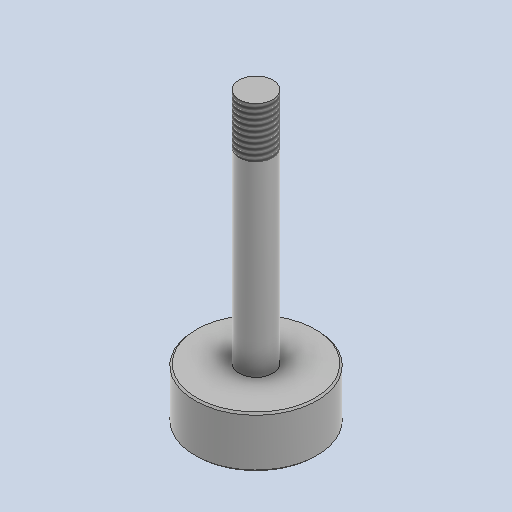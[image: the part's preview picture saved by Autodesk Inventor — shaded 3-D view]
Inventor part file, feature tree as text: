
AUTODESK INVENTOR PART (.ipt)
format: ipt  version: 2023 (Build 270158000, 158)  size: 279,040 bytes
history: native  units: mm
features: extrude x2, chamfer x2, sketch x2, other x1, thread x1
ambient origin geometry x8: Origin, YZ Plane, XZ Plane, XY Plane, X Axis, Y Axis, Z Axis, Center Point
bodies: Body1 (feature_tree)
feature tree (8):
  other  "Sólido1"
  extrude  "Extrusão1"  Depth=15.0mm TaperAngle=0.0deg
  extrude  "Extrusão2"  Depth=70.0mm TaperAngle=0.0deg
  thread  "Rosca1"  [1 undecoded]
  chamfer  "Chamfer1"  Distance=0.5mm Angle=45.0deg
  chamfer  "Chamfer2"  Distance=0.5mm Angle=45.0deg
  sketch  "Esboço1"  dims[d0=36.0mm d1=15.0mm d2=0.0mm]
  sketch  "Esboço2"  dims[d3=10.0mm d4=70.0mm d5=0.0mm d6=15.0mm d7=55.0mm d8=0.5mm d9=2.0mm d10=45.0deg d11=0.5mm d12=2.0mm d13=45.0deg]
note: 1 required parameter value undecoded (feature->parameter linkage not recoverable at this tier; creation-order binding heuristic only, values carry confidence <= 0.55)
